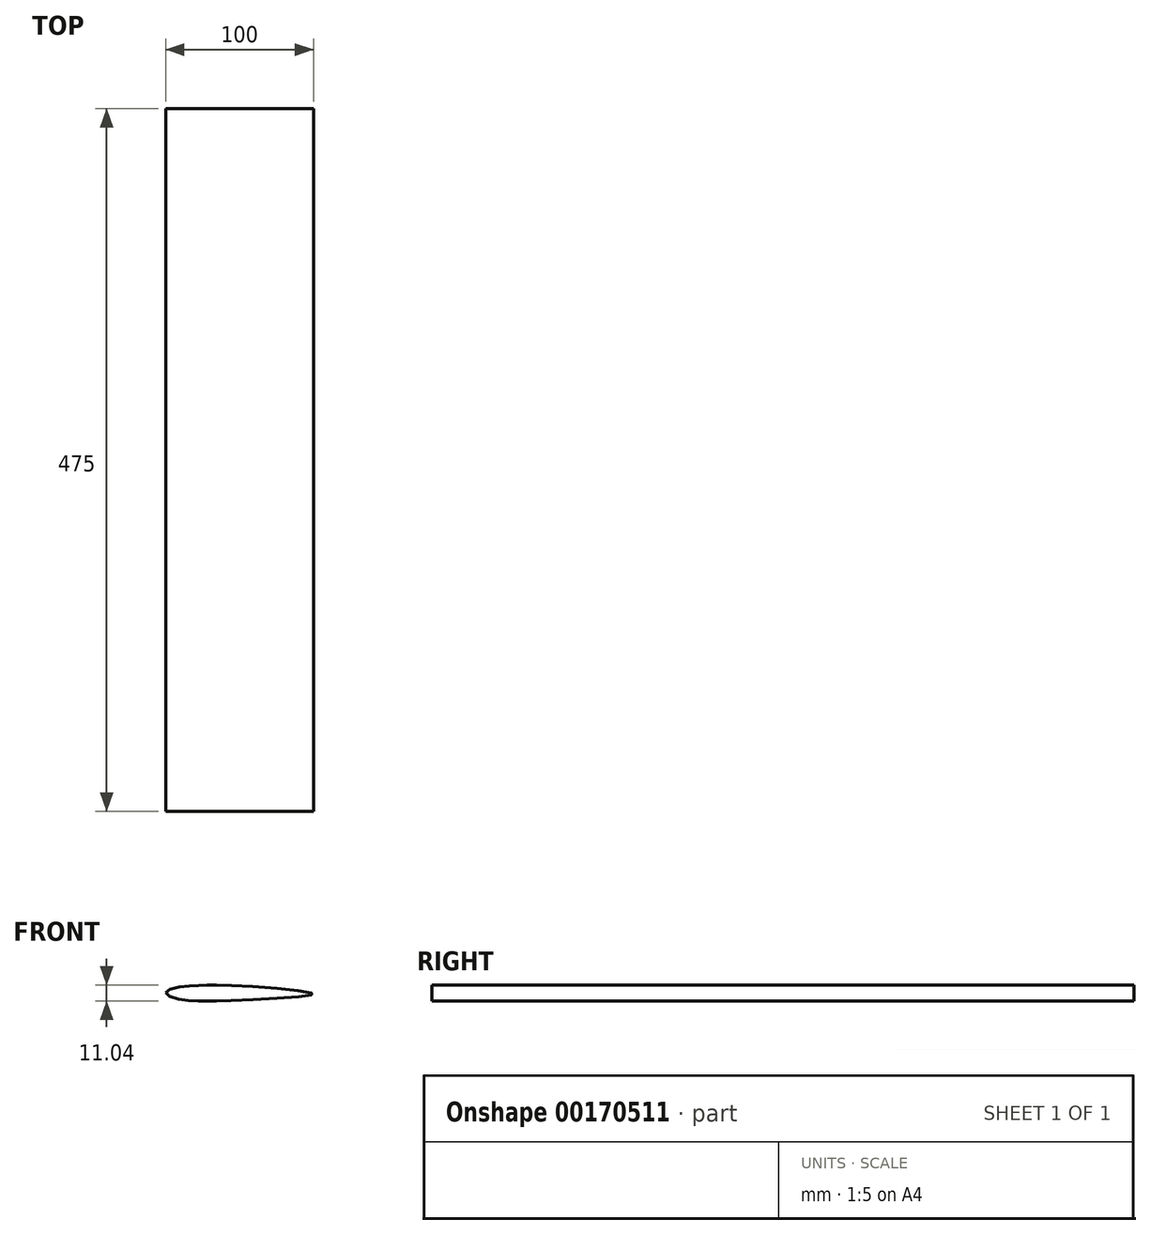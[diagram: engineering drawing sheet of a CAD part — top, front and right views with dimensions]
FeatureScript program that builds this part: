
annotation { "Feature Type Name" : "Feature", "Feature Type Description" : "" }
export const myFeature = defineFeature(function(context is Context, id is Id, definition is map)
    precondition{}
    {
        {
            var Q0;
            Q0=qCreatedBy(makeId("Front.planeOp"),FACE);
            var sketch = newSketch(context, id + "F0", { "sketchPlane" : qUnion([Q0])});
            skFitSpline(sketch, "E0", {"points": [v(-107.88, -15.8) * mm, v(-100.07, -12.4) * mm, v(-84.46, -10.93) * mm, v(-64.46, -10.93) * mm, v(-7.88, -16.78) * mm, v(-65.44, -21.17) * mm, v(-84.95, -21.66) * mm, v(-101.54, -19.71) * mm, v(-107.88, -15.8) * mm]});
            skSolve(sketch);
        }
        {
            var Q0;
            Q0 = qSketchRegion(id + "F0", true);
            extrude(context, id + "F1", {"entities" : qUnion([Q0]), "depth" : 25 * mm});
        }
        {
            var Q0;
            Q0=makeQuery(id+"F1.opExtrude","CAP_FACE",FACE,{"disambiguationData":[OSD([sQuery(id+"F0.wireOp",EDGE,"E0")])],"isStart":false});
            extrude(context, id + "F2", {"entities" : qUnion([Q0]), "operationType" : NewBodyOperationType.ADD, "depth" : 450 * mm});
        }
    });
